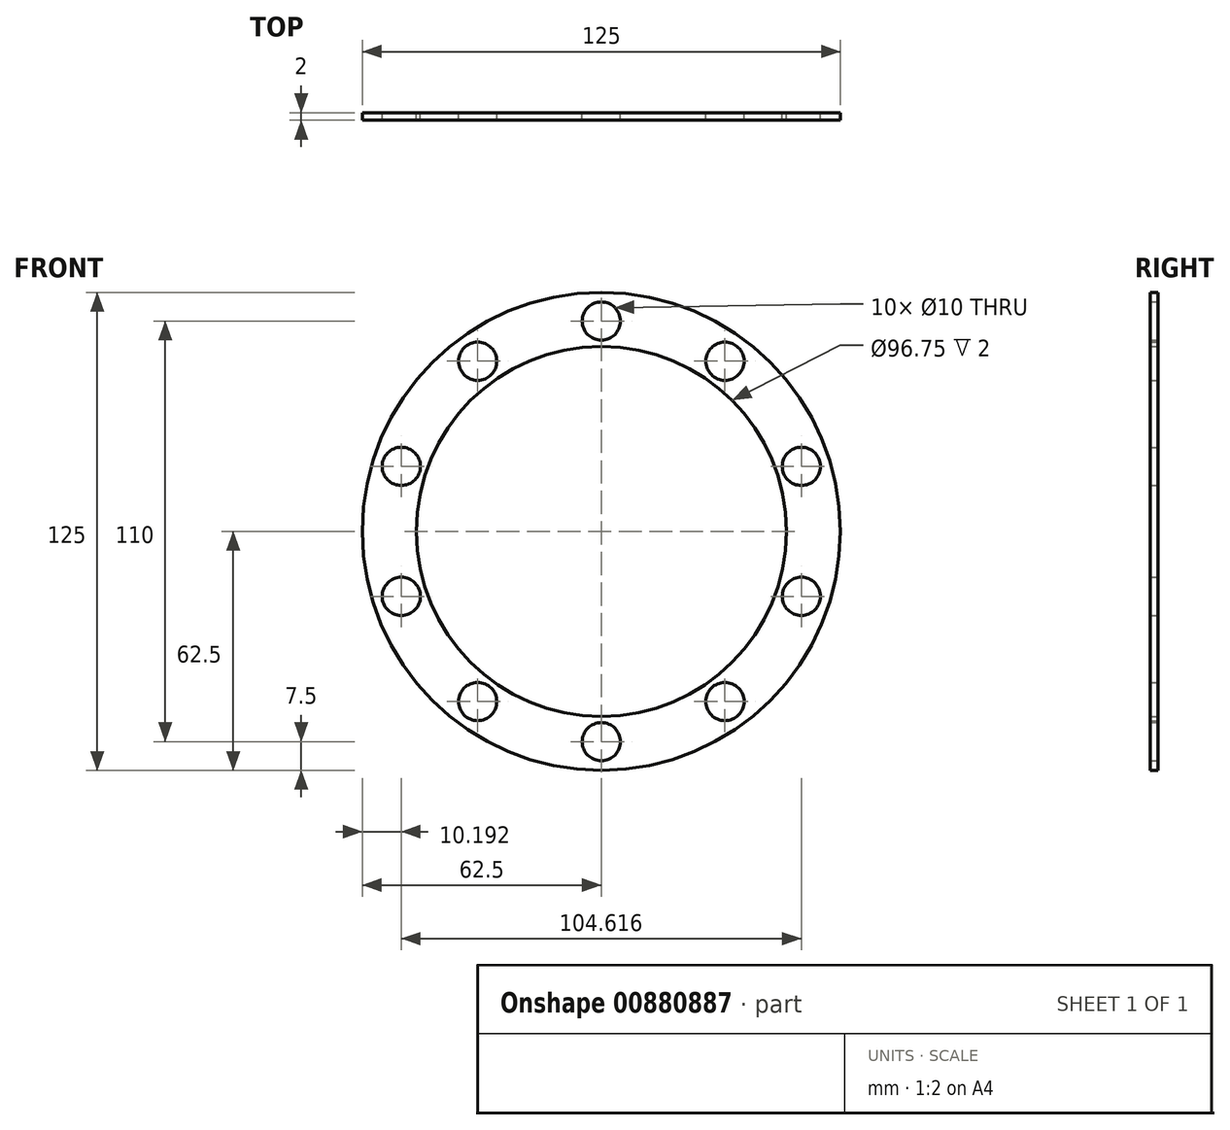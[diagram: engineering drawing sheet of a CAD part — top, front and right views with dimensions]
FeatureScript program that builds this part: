
annotation { "Feature Type Name" : "Feature", "Feature Type Description" : "" }
export const myFeature = defineFeature(function(context is Context, id is Id, definition is map)
    precondition{}
    {
        {
            var Q0;
            Q0=qCreatedBy(makeId("Front.planeOp"),FACE);
            var sketch = newSketch(context, id + "F0", { "sketchPlane" : qUnion([Q0])});
            skCircle(sketch, "E0", {"center": v(0, 0) * mm, "radius": 55 * mm, "construction": true});
            skPoint(sketch, "E1.center", {"position": v(8.22, 0) * mm});
            skCircle(sketch, "E2", {"center": v(0, 0) * mm, "radius": 48.38 * mm});
            skPoint(sketch, "E3.center.orphan", {"position": v(0, 55) * mm});
            skCircle(sketch, "E4", {"center": v(0, 55) * mm, "radius": 5 * mm});
            skCircle(sketch, "E5.1.0", {"center": v(-32.33, 44.5) * mm, "radius": 5 * mm});
            skCircle(sketch, "E5.2.0", {"center": v(-52.3, 17) * mm, "radius": 5 * mm});
            skCircle(sketch, "E5.3.0", {"center": v(-52.3, -17) * mm, "radius": 5 * mm});
            skCircle(sketch, "E5.4.0", {"center": v(-32.33, -44.5) * mm, "radius": 5 * mm});
            skCircle(sketch, "E5.5.0", {"center": v(0, -55) * mm, "radius": 5 * mm});
            skCircle(sketch, "E5.6.0", {"center": v(32.33, -44.5) * mm, "radius": 5 * mm});
            skCircle(sketch, "E5.7.0", {"center": v(52.3, -17) * mm, "radius": 5 * mm});
            skCircle(sketch, "E5.8.0", {"center": v(52.3, 17) * mm, "radius": 5 * mm});
            skCircle(sketch, "E5.9.0", {"center": v(32.33, 44.5) * mm, "radius": 5 * mm});
            skCircle(sketch, "E6", {"center": v(0, 0) * mm, "radius": 62.5 * mm});
            skLineSegment(sketch, "E7", {"start": v(0, 55) * mm, "end": v(0, 0) * mm});
            skLineSegment(sketch, "E8", {"start": v(32.33, 44.5) * mm, "end": v(0, 0) * mm});
            skSolve(sketch);
        }
        {
            var Q0;
            Q0 = qSketchRegion(id + "F0", true);
            extrude(context, id + "F1", {"entities" : qUnion([Q0]), "endBound" : BoundingType.SYMMETRIC, "depth" : 2 * mm, "offsetDistance" : 25 * mm});
        }
    });
